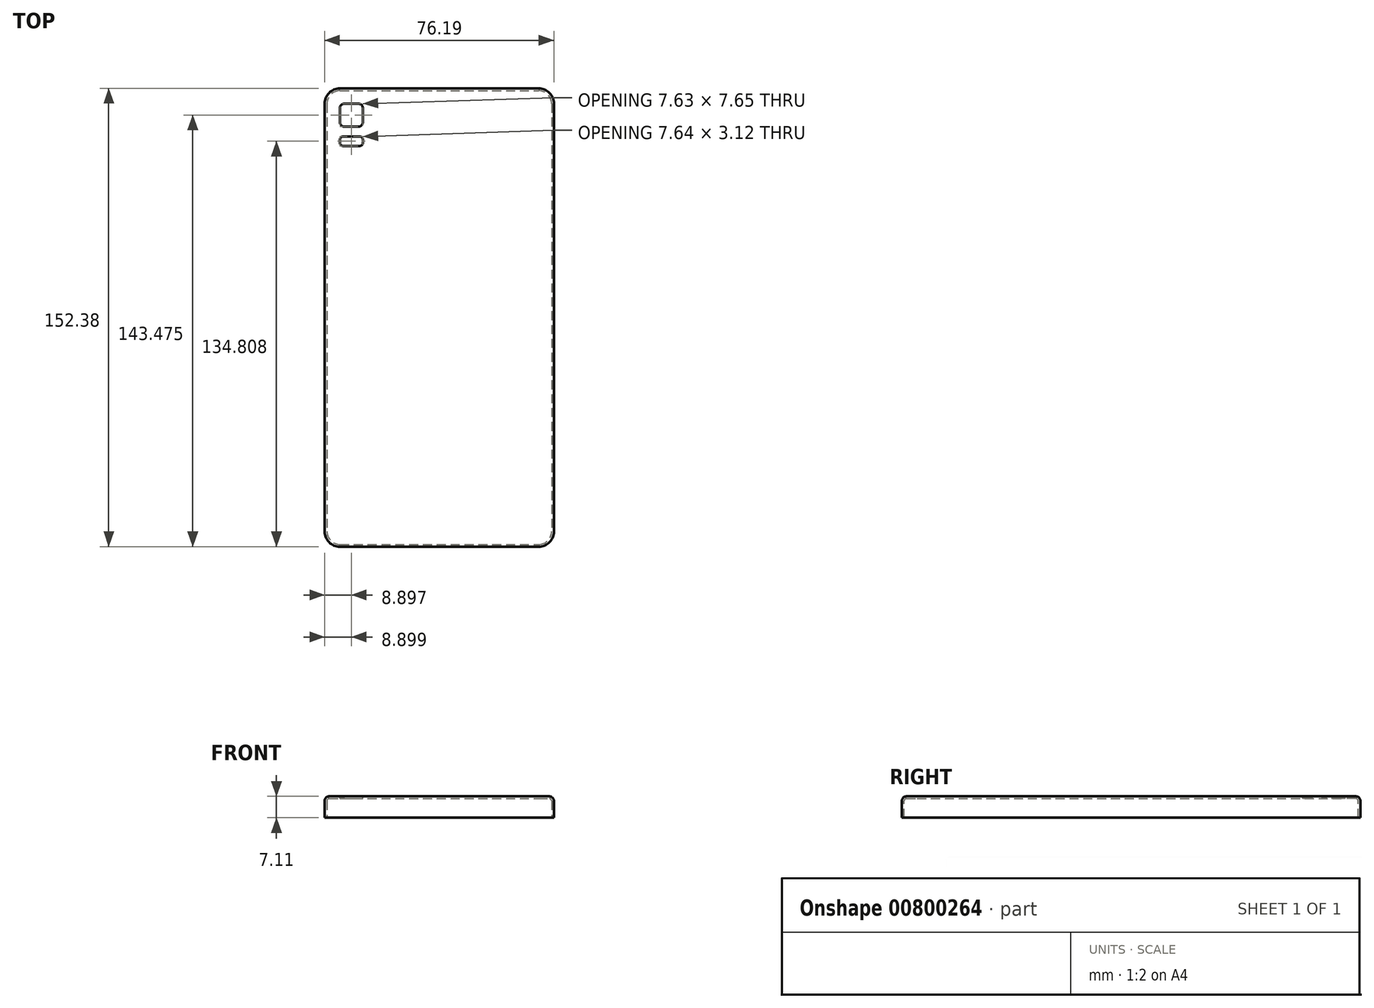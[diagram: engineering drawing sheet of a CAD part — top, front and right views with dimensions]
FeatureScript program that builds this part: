
annotation { "Feature Type Name" : "Feature", "Feature Type Description" : "" }
export const myFeature = defineFeature(function(context is Context, id is Id, definition is map)
    precondition{}
    {
        {
            var Q0;
            Q0=qCreatedBy(makeId("Top.planeOp"),FACE);
            var sketch = newSketch(context, id + "F0", { "sketchPlane" : qUnion([Q0])});
            skLineSegment(sketch, "E0.bottom", {"start": v(-35.6, 73.42) * mm, "end": v(40.58, 73.42) * mm});
            skLineSegment(sketch, "E0.top", {"start": v(-35.6, -78.96) * mm, "end": v(40.58, -78.96) * mm});
            skLineSegment(sketch, "E0.left", {"start": v(-35.6, 73.42) * mm, "end": v(-35.6, -78.96) * mm});
            skLineSegment(sketch, "E0.right", {"start": v(40.58, 73.42) * mm, "end": v(40.58, -78.96) * mm});
            skSolve(sketch);
        }
        {
            var Q0;
            Q0=makeQuery(id+"F0.imprint","IMPRINT",FACE,{"disambiguationData":[TD([[makeQuery(id+"F0.imprint","IMPRINT",EDGE,{"derivedFrom":sQuery(id+"F0.wireOp",EDGE,"E0.bottom")}),-1.0]])]});
            extrude(context, id + "F1", {"entities" : qUnion([Q0]), "depth" : 7.11 * mm, "offsetDistance" : 25.4 * mm});
        }
        {
            var Q0;
            Q0=makeQuery(id+"F1.opExtrude","SWEPT_EDGE",EDGE,{"disambiguationData":[OSD([sQuery(id+"F0.wireOp",EDGE,"E0.top"),sQuery(id+"F0.wireOp",EDGE,"E0.right")])]});
            var Q1;
            Q1=makeQuery(id+"F1.opExtrude","SWEPT_EDGE",EDGE,{"disambiguationData":[OSD([sQuery(id+"F0.wireOp",EDGE,"E0.top"),sQuery(id+"F0.wireOp",EDGE,"E0.left")])]});
            var Q2;
            Q2=makeQuery(id+"F1.opExtrude","SWEPT_EDGE",EDGE,{"disambiguationData":[OSD([sQuery(id+"F0.wireOp",EDGE,"E0.bottom"),sQuery(id+"F0.wireOp",EDGE,"E0.left")])]});
            var Q3;
            Q3=makeQuery(id+"F1.opExtrude","SWEPT_EDGE",EDGE,{"disambiguationData":[OSD([sQuery(id+"F0.wireOp",EDGE,"E0.bottom"),sQuery(id+"F0.wireOp",EDGE,"E0.right")])]});
            fillet(context, id + "F2", {"entities" : qUnion([Q0, Q1, Q2, Q3]), "radius" : 5.08 * mm, "tangentPropagation" : true, "allowEdgeOverflow" : false});
        }
        {
            var Q0;
            Q0=makeQuery(id+"F1.opExtrude","CAP_EDGE",EDGE,{"disambiguationData":[OSD([sQuery(id+"F0.wireOp",EDGE,"E0.right")])],"isStart":false});
            var Q1;
            Q1=makeQuery(id+"F1.opExtrude","CAP_EDGE",EDGE,{"disambiguationData":[OSD([sQuery(id+"F0.wireOp",EDGE,"E0.left")])],"isStart":false});
            fillet(context, id + "F3", {"entities" : qUnion([Q0, Q1]), "radius" : 1.52 * mm, "tangentPropagation" : true, "allowEdgeOverflow" : false});
        }
        {
            var Q0;
            Q0=makeQuery(id+"F1.opExtrude","CAP_FACE",FACE,{"disambiguationData":[OSD([sQuery(id+"F0.wireOp",EDGE,"E0.bottom"),sQuery(id+"F0.wireOp",EDGE,"E0.top"),sQuery(id+"F0.wireOp",EDGE,"E0.left"),sQuery(id+"F0.wireOp",EDGE,"E0.right")])],"isStart":true});
            shell(context, id + "F4", {"entities" : qUnion([Q0]), "thickness" : 0.76 * mm});
        }
        {
            var Q0;
            Q0=makeQuery(id+"F1.opExtrude","CAP_FACE",FACE,{"disambiguationData":[OSD([sQuery(id+"F0.wireOp",EDGE,"E0.bottom"),sQuery(id+"F0.wireOp",EDGE,"E0.top"),sQuery(id+"F0.wireOp",EDGE,"E0.left"),sQuery(id+"F0.wireOp",EDGE,"E0.right")])],"isStart":false});
            var sketch = newSketch(context, id + "F5", { "sketchPlane" : qUnion([Q0])});
            skLineSegment(sketch, "E1.bottom", {"start": v(-30.53, 68.34) * mm, "end": v(-22.9, 68.34) * mm});
            skLineSegment(sketch, "E1.top", {"start": v(-30.53, 60.7) * mm, "end": v(-22.9, 60.7) * mm});
            skLineSegment(sketch, "E1.left", {"start": v(-30.53, 68.34) * mm, "end": v(-30.53, 60.7) * mm});
            skLineSegment(sketch, "E1.right", {"start": v(-22.9, 68.34) * mm, "end": v(-22.9, 60.7) * mm});
            skSolve(sketch);
        }
        {
            var Q0;
            Q0=makeQuery(id+"F5.imprint","IMPRINT",FACE,{"disambiguationData":[TD([[makeQuery(id+"F5.imprint","IMPRINT",EDGE,{"derivedFrom":sQuery(id+"F5.wireOp",EDGE,"E1.bottom")}),-1.0]])]});
            extrude(context, id + "F6", {"entities" : qUnion([Q0]), "operationType" : NewBodyOperationType.REMOVE, "oppositeDirection" : true, "depth" : 25.4 * mm, "offsetDistance" : 25.4 * mm});
        }
        {
            var Q0;
            Q0=makeQuery(id+"F6.boolean.opBoolean","COPY",EDGE,{"derivedFrom":makeQuery(id+"F6.opExtrude","SWEPT_EDGE",EDGE,{"disambiguationData":[OSD([sQuery(id+"F5.wireOp",EDGE,"E1.top"),sQuery(id+"F5.wireOp",EDGE,"E1.right")])]})});
            var Q1;
            Q1=makeQuery(id+"F6.boolean.opBoolean","COPY",EDGE,{"derivedFrom":makeQuery(id+"F6.opExtrude","SWEPT_EDGE",EDGE,{"disambiguationData":[OSD([sQuery(id+"F5.wireOp",EDGE,"E1.top"),sQuery(id+"F5.wireOp",EDGE,"E1.left")])]})});
            var Q2;
            Q2=makeQuery(id+"F6.boolean.opBoolean","COPY",EDGE,{"derivedFrom":makeQuery(id+"F6.opExtrude","SWEPT_EDGE",EDGE,{"disambiguationData":[OSD([sQuery(id+"F5.wireOp",EDGE,"E1.bottom"),sQuery(id+"F5.wireOp",EDGE,"E1.right")])]})});
            var Q3;
            Q3=makeQuery(id+"F6.boolean.opBoolean","COPY",EDGE,{"derivedFrom":makeQuery(id+"F6.opExtrude","SWEPT_EDGE",EDGE,{"disambiguationData":[OSD([sQuery(id+"F5.wireOp",EDGE,"E1.bottom"),sQuery(id+"F5.wireOp",EDGE,"E1.left")])]})});
            fillet(context, id + "F7", {"entities" : qUnion([Q0, Q1, Q2, Q3]), "radius" : 1.52 * mm, "tangentPropagation" : true, "allowEdgeOverflow" : false});
        }
        {
            var Q0;
            Q0=makeQuery(id+"F1.opExtrude","CAP_FACE",FACE,{"disambiguationData":[OSD([sQuery(id+"F0.wireOp",EDGE,"E0.bottom"),sQuery(id+"F0.wireOp",EDGE,"E0.top"),sQuery(id+"F0.wireOp",EDGE,"E0.left"),sQuery(id+"F0.wireOp",EDGE,"E0.right")])],"isStart":false});
            var sketch = newSketch(context, id + "F8", { "sketchPlane" : qUnion([Q0])});
            skLineSegment(sketch, "E2.bottom", {"start": v(-30.53, 57.4) * mm, "end": v(-22.9, 57.4) * mm});
            skLineSegment(sketch, "E2.top", {"start": v(-30.53, 54.29) * mm, "end": v(-22.9, 54.29) * mm});
            skLineSegment(sketch, "E2.left", {"start": v(-30.53, 57.4) * mm, "end": v(-30.53, 54.29) * mm});
            skLineSegment(sketch, "E2.right", {"start": v(-22.9, 57.4) * mm, "end": v(-22.9, 54.29) * mm});
            skPoint(sketch, "E3", {"position": v(21.93, 66.05) * mm});
            skSolve(sketch);
        }
        {
            var Q0;
            Q0 = qSketchRegion(id + "F8", true);
            extrude(context, id + "F9", {"entities" : qUnion([Q0]), "operationType" : NewBodyOperationType.REMOVE, "oppositeDirection" : true, "depth" : 25.4 * mm, "offsetDistance" : 25.4 * mm});
        }
        {
            var Q0;
            Q0=makeQuery(id+"F9.boolean.opBoolean","COPY",EDGE,{"derivedFrom":makeQuery(id+"F9.opExtrude","SWEPT_EDGE",EDGE,{"disambiguationData":[OSD([sQuery(id+"F8.wireOp",EDGE,"E2.top"),sQuery(id+"F8.wireOp",EDGE,"E2.left")])]})});
            var Q1;
            Q1=makeQuery(id+"F9.boolean.opBoolean","COPY",EDGE,{"derivedFrom":makeQuery(id+"F9.opExtrude","SWEPT_EDGE",EDGE,{"disambiguationData":[OSD([sQuery(id+"F8.wireOp",EDGE,"E2.top"),sQuery(id+"F8.wireOp",EDGE,"E2.right")])]})});
            var Q2;
            Q2=makeQuery(id+"F9.boolean.opBoolean","COPY",EDGE,{"derivedFrom":makeQuery(id+"F9.opExtrude","SWEPT_EDGE",EDGE,{"disambiguationData":[OSD([sQuery(id+"F8.wireOp",EDGE,"E2.bottom"),sQuery(id+"F8.wireOp",EDGE,"E2.left")])]})});
            var Q3;
            Q3=makeQuery(id+"F9.boolean.opBoolean","COPY",EDGE,{"derivedFrom":makeQuery(id+"F9.opExtrude","SWEPT_EDGE",EDGE,{"disambiguationData":[OSD([sQuery(id+"F8.wireOp",EDGE,"E2.bottom"),sQuery(id+"F8.wireOp",EDGE,"E2.right")])]})});
            fillet(context, id + "F10", {"entities" : qUnion([Q0, Q1, Q2, Q3]), "radius" : 1.02 * mm, "tangentPropagation" : true, "allowEdgeOverflow" : false});
        }
    });
